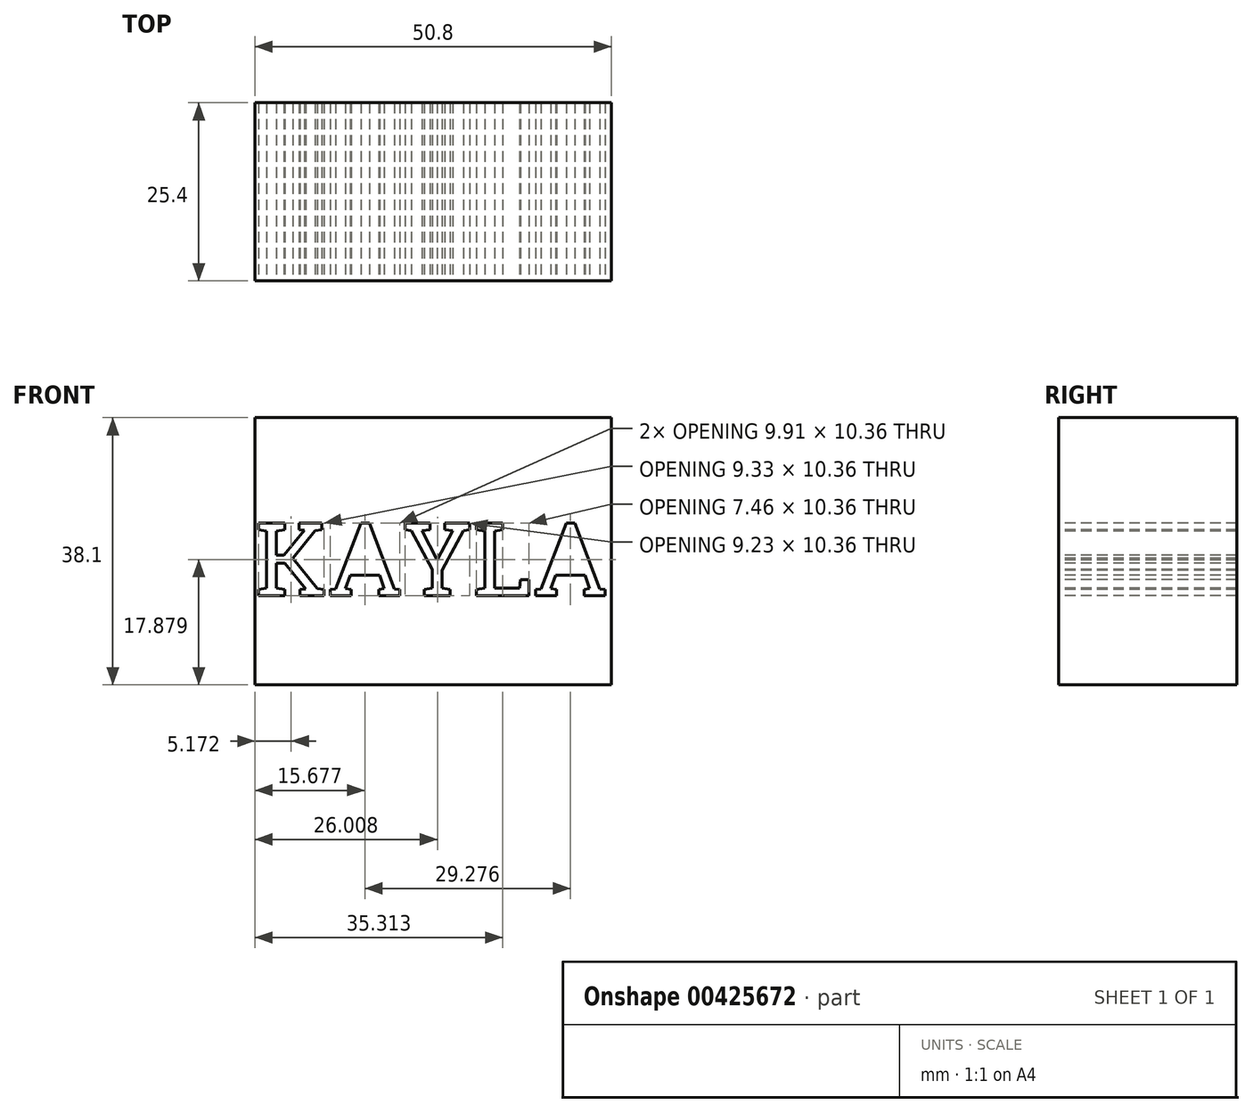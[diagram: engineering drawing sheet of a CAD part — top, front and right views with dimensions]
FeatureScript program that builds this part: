
annotation { "Feature Type Name" : "Feature", "Feature Type Description" : "" }
export const myFeature = defineFeature(function(context is Context, id is Id, definition is map)
    precondition{}
    {
        {
            var Q0;
            Q0=qCreatedBy(makeId("Front.planeOp"),FACE);
            var sketch = newSketch(context, id + "F0", { "sketchPlane" : qUnion([Q0])});
            skLineSegment(sketch, "E0", {"start": v(-39.12, 38.1) * mm, "end": v(-39.12, 0) * mm});
            skLineSegment(sketch, "E1", {"start": v(-39.12, 0) * mm, "end": v(11.68, 0) * mm});
            skLineSegment(sketch, "E2", {"start": v(11.68, 0) * mm, "end": v(11.68, 38.1) * mm});
            skLineSegment(sketch, "E3", {"start": v(11.68, 38.1) * mm, "end": v(-39.12, 38.1) * mm});
            skText(sketch, "E4", { "text": "KAYLA", "fontName": "RobotoSlab-Regular.ttf"});
            const initialGuessF0  = {"E4": [-0.03912, 0.0127, 1, 0, 0.01049]};
            skSetInitialGuess(sketch, initialGuessF0);
            skSolve(sketch);
        }
        {
            var Q0;
            Q0=makeQuery(id+"F0.imprint","IMPRINT",FACE,{"disambiguationData":[TD([[makeQuery(id+"F0.imprint","IMPRINT",EDGE,{"derivedFrom":sQuery(id+"F0.wireOp",EDGE,"E0")}),1.0]])]});
            extrude(context, id + "F1", {"entities" : qUnion([Q0]), "oppositeDirection" : true, "depth" : 25.4 * mm});
        }
    });
